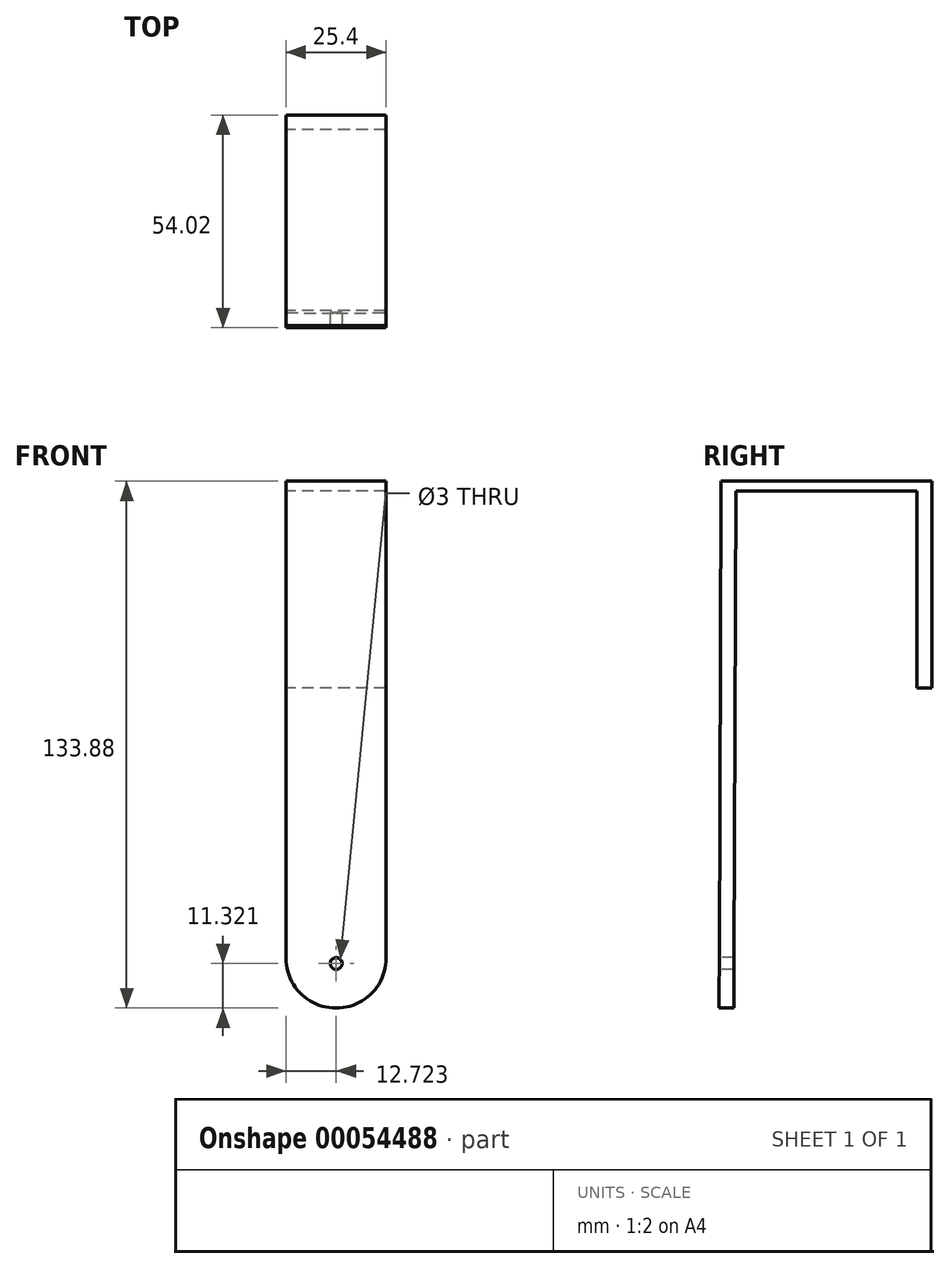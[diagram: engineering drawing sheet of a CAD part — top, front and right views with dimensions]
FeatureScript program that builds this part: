
annotation { "Feature Type Name" : "Feature", "Feature Type Description" : "" }
export const myFeature = defineFeature(function(context is Context, id is Id, definition is map)
    precondition{}
    {
        {
            var Q0;
            Q0=qCreatedBy(makeId("Right.planeOp"),FACE);
            var sketch = newSketch(context, id + "F0", { "sketchPlane" : qUnion([Q0])});
            skLineSegment(sketch, "E0", {"start": v(-48.1, 20.88) * mm, "end": v(-2.1, 20.88) * mm});
            skLineSegment(sketch, "E1", {"start": v(-2.1, 20.88) * mm, "end": v(-2.1, -29.12) * mm});
            skLineSegment(sketch, "E2.bottom", {"start": v(-52.37, -110.46) * mm, "end": v(-48.62, -110.46) * mm});
            skLineSegment(sketch, "E2.left", {"start": v(-52.37, -110.46) * mm, "end": v(-51.85, 20.97) * mm});
            skLineSegment(sketch, "E2.right", {"start": v(-48.62, -110.46) * mm, "end": v(-48.1, 20.88) * mm});
            skLineSegment(sketch, "E3.top", {"start": v(-51.85, 23.42) * mm, "end": v(1.65, 23.42) * mm});
            skLineSegment(sketch, "E3.left", {"start": v(-51.85, 20.97) * mm, "end": v(-51.85, 23.42) * mm});
            skLineSegment(sketch, "E3.right", {"start": v(1.65, 20.88) * mm, "end": v(1.65, 23.42) * mm});
            skLineSegment(sketch, "E4.top", {"start": v(1.65, -29.12) * mm, "end": v(-2.1, -29.12) * mm});
            skLineSegment(sketch, "E4.left", {"start": v(1.65, 20.88) * mm, "end": v(1.65, -29.12) * mm});
            skLineSegment(sketch, "E5", {"start": v(-2.1, 20.88) * mm, "end": v(1.65, 20.88) * mm});
            skLineSegment(sketch, "E6", {"start": v(-51.85, 20.97) * mm, "end": v(-48.1, 20.88) * mm});
            skSolve(sketch);
        }
        {
            var Q0;
            Q0 = qSketchRegion(id + "F0", true);
            extrude(context, id + "F1", {"entities" : qUnion([Q0]), "depth" : 25.4 * mm});
        }
        {
            var Q0;
            Q0=makeQuery(id+"F1.opExtrude","SWEPT_FACE",FACE,{"disambiguationData":[OSD([sQuery(id+"F0.wireOp",EDGE,"E2.left"),sQuery(id+"F0.wireOp",EDGE,"E3.left")])]});
            var sketch = newSketch(context, id + "F2", { "sketchPlane" : qUnion([Q0])});
            skCircle(sketch, "E7", {"center": v(12.72, -99.34) * mm, "radius": 1.5 * mm});
            skSolve(sketch);
        }
        {
            var Q0;
            Q0 = qSketchRegion(id + "F2", true);
            extrude(context, id + "F3", {"entities" : qUnion([Q0]), "operationType" : NewBodyOperationType.REMOVE, "oppositeDirection" : true, "depth" : 3.75 * mm});
        }
        {
            var Q0;
            Q0=makeQuery(id+"F1.opExtrude","CAP_EDGE",EDGE,{"disambiguationData":[OSD([sQuery(id+"F0.wireOp",EDGE,"E2.bottom")])],"isStart":false});
            var Q1;
            Q1=makeQuery(id+"F1.opExtrude","CAP_EDGE",EDGE,{"disambiguationData":[OSD([sQuery(id+"F0.wireOp",EDGE,"E2.bottom")])],"isStart":true});
            fillet(context, id + "F4", {"entities" : qUnion([Q0, Q1]), "radius" : 12.65 * mm, "tangentPropagation" : true, "allowEdgeOverflow" : false});
        }
    });
